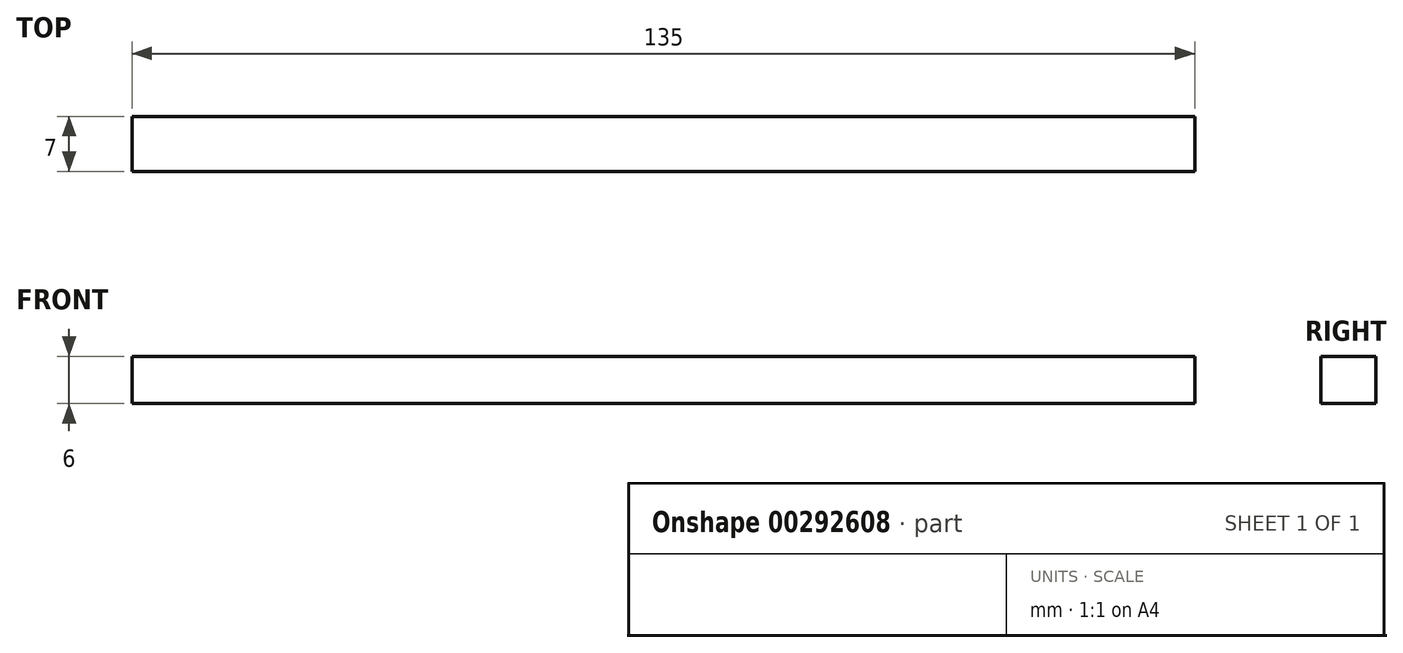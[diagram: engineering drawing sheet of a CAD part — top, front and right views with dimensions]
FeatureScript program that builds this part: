
annotation { "Feature Type Name" : "Feature", "Feature Type Description" : "" }
export const myFeature = defineFeature(function(context is Context, id is Id, definition is map)
    precondition{}
    {
        {
            var Q0;
            Q0=qCreatedBy(makeId("Front.planeOp"),FACE);
            var sketch = newSketch(context, id + "F0", { "sketchPlane" : qUnion([Q0])});
            skLineSegment(sketch, "E0", {"start": v(0, 6) * mm, "end": v(67.5, 6) * mm});
            skLineSegment(sketch, "E1", {"start": v(67.5, 6) * mm, "end": v(67.5, 0) * mm});
            skLineSegment(sketch, "E2.MirrorCS", {"start": v(0, 6) * mm, "end": v(-67.5, 6) * mm});
            skLineSegment(sketch, "E3.MirrorCS", {"start": v(-67.5, 6) * mm, "end": v(-67.5, 0) * mm});
            skLineSegment(sketch, "E4", {"start": v(-67.5, 0) * mm, "end": v(67.5, 0) * mm});
            skSolve(sketch);
        }
        {
            var Q0;
            Q0 = qSketchRegion(id + "F0", true);
            extrude(context, id + "F1", {"entities" : qUnion([Q0]), "endBound" : BoundingType.SYMMETRIC, "depth" : 7 * mm});
        }
    });
